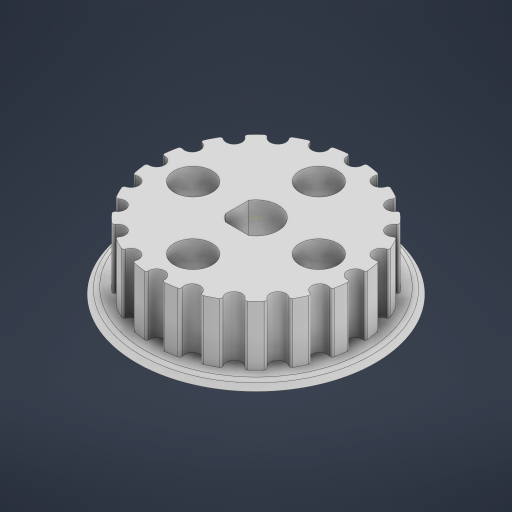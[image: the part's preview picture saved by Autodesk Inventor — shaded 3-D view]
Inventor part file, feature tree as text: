
AUTODESK INVENTOR PART (.ipt)
format: ipt  version: 2024 (Build 280153000, 153)  size: 420,864 bytes
history: native  units: mm
features: sketch x5, extrude x4, fillet x2, chamfer x1, pattern_circular x1
ambient origin geometry x8: Origin, YZ Plane, XZ Plane, XY Plane, X Axis, Y Axis, Z Axis, Center Point
bodies: Solid1 (feature_tree)
feature tree (13):
  extrude  "Extrusion1"  Depth=21.0mm TaperAngle=0.0deg
  extrude  "Extrusion2"  Depth=2.0mm
  chamfer  "Chamfer1"  Distance=2.0mm Angle=45.0deg
  fillet  "Fillet1"  Radius=2.0mm
  extrude  "Extrusion3"  Depth=6.0mm
  extrude  "Extrusion4"  Depth=5.0mm
  pattern_circular  "Circular Pattern1"  [2 undecoded]
  fillet  "Fillet2"  Radius=200.0mm
  sketch  "Sketch5"  dims[d15=31.6mm d16=19.0mm d17=0.0mm d18=200.0mm d19=360.0deg d21=0.7mm d23=6.0mm d24=20.0mm d25=20.0mm d26=20.0mm d27=20.0mm]
  sketch  "Sketch1"  dims[d0=65.0mm d1=21.0mm d2=0.0mm]
  sketch  "Sketch2"  dims[d3=2.0mm d4=0.0mm d5=76.0mm d6=2.0mm d7=2.0mm d8=45.0deg d9=2.0mm]
  sketch  "Sketch3"  dims[d10=14.1mm d11=6.0mm]
  sketch  "Sketch4"  dims[d12=40.0mm d13=0.0mm d14=5.0mm]
note: 2 required parameter values undecoded (feature->parameter linkage not recoverable at this tier; creation-order binding heuristic only, values carry confidence <= 0.55)
